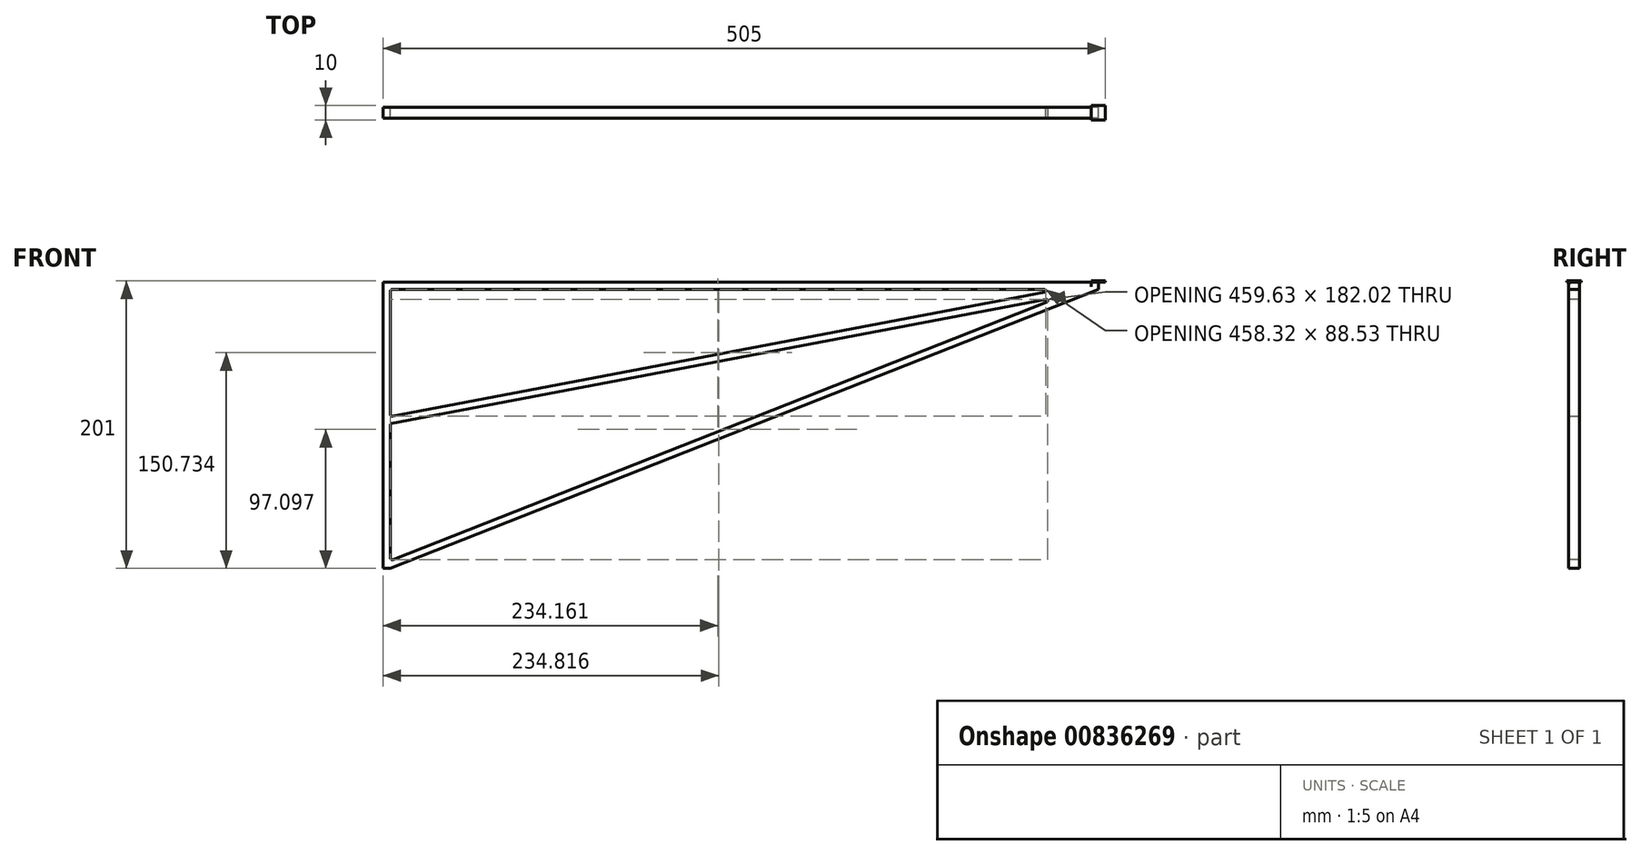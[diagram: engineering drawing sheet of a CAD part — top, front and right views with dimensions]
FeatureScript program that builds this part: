
annotation { "Feature Type Name" : "Feature", "Feature Type Description" : "" }
export const myFeature = defineFeature(function(context is Context, id is Id, definition is map)
    precondition{}
    {
        {
            var Q0;
            Q0=qCreatedBy(makeId("Front.planeOp"),FACE);
            var sketch = newSketch(context, id + "F0", { "sketchPlane" : qUnion([Q0])});
            skLineSegment(sketch, "E0.bottom", {"start": v(-27.04, 0) * mm, "end": v(-495, 0) * mm});
            skLineSegment(sketch, "E0.top", {"start": v(0, 5) * mm, "end": v(-500, 5) * mm});
            skLineSegment(sketch, "E0.left", {"start": v(0, 0) * mm, "end": v(0, 5) * mm});
            skLineSegment(sketch, "E0.right", {"start": v(-500, 0) * mm, "end": v(-500, 5) * mm});
            skLineSegment(sketch, "E1.bottom", {"start": v(-500, 5) * mm, "end": v(-495, 5) * mm});
            skLineSegment(sketch, "E1.top", {"start": v(-500, -195) * mm, "end": v(-495, -195) * mm});
            skLineSegment(sketch, "E1.left", {"start": v(-500, 5) * mm, "end": v(-500, -195) * mm});
            skLineSegment(sketch, "E1.right", {"start": v(-495, 0) * mm, "end": v(-495, -88.84) * mm});
            skLineSegment(sketch, "E2", {"start": v(-495, -195) * mm, "end": v(0, 0) * mm});
            skPoint(sketch, "E3", {"position": v(-495, -189.63) * mm});
            skLineSegment(sketch, "E4", {"start": v(-495, -189.63) * mm, "end": v(-26.11, -4.91) * mm});
            skPoint(sketch, "E5", {"position": v(-147.96, -25.5) * mm});
            skLineSegment(sketch, "E6", {"start": v(-13.64, 0) * mm, "end": v(-14.6, 5) * mm});
            skPoint(sketch, "E7", {"position": v(-14.1, 2.46) * mm});
            skLineSegment(sketch, "E8", {"start": v(-27.04, 0) * mm, "end": v(-495, -88.84) * mm});
            skLineSegment(sketch, "E9", {"start": v(-494.07, -93.76) * mm, "end": v(-26.11, -4.91) * mm});
            skLineSegment(sketch, "E10.trimOffspring", {"start": v(-495, -95.28) * mm, "end": v(-495, -189.63) * mm});
            skLineSegment(sketch, "E11", {"start": v(-408.19, -160.8) * mm, "end": v(-410.02, -156.15) * mm});
            skLineSegment(sketch, "E12", {"start": v(-495, -142.45) * mm, "end": v(-26.11, -4.91) * mm});
            skLineSegment(sketch, "E13", {"start": v(-495, -44.42) * mm, "end": v(-27.04, 0) * mm});
            skLineSegment(sketch, "E14", {"start": v(-495, -95.28) * mm, "end": v(-495, -93.93) * mm});
            skLineSegment(sketch, "E15", {"start": v(-494.07, -93.76) * mm, "end": v(-495, -93.93) * mm});
            skPoint(sketch, "E16.orphan", {"position": v(-495, -93.76) * mm});
            skSolve(sketch);
        }
        {
            var Q0;
            {var subQ6=sQuery(id+"F0.wireOp",EDGE,"E0.bottom");Q0=makeQuery(id+"F0.imprint","IMPRINT",FACE,{"disambiguationData":[TD([[makeQuery(id+"F0.imprint","IMPRINT",EDGE,{"derivedFrom":subQ6}),-1.0]])]});}
            extrude(context, id + "F1", {"entities" : qUnion([Q0]), "depth" : 7.5 * mm, "offsetDistance" : 25 * mm});
        }
        {
            var Q0;
            Q0=makeQuery(id+"F1.opExtrude","SWEPT_EDGE",EDGE,{"disambiguationData":[OSD([sQuery(id+"F0.wireOp",EDGE,"E1.right"),sQuery(id+"F0.wireOp",EDGE,"E8")])]});
            fillet(context, id + "F2", {"entities" : qUnion([Q0]), "radius" : 1.5 * mm, "tangentPropagation" : true, "allowEdgeOverflow" : false});
        }
        {
            var Q0;
            Q0=makeQuery(id+"F1.opExtrude","SWEPT_EDGE",EDGE,{"disambiguationData":[OSD([sQuery(id+"F0.wireOp",EDGE,"E14"),sQuery(id+"F0.wireOp",EDGE,"E15")])]});
            var Q1;
            Q1=makeQuery(id+"F1.opExtrude","SWEPT_EDGE",EDGE,{"disambiguationData":[OSD([sQuery(id+"F0.wireOp",EDGE,"E0.bottom"),sQuery(id+"F0.wireOp",EDGE,"E1.right")])]});
            var Q2;
            Q2=makeQuery(id+"F1.opExtrude","SWEPT_EDGE",EDGE,{"disambiguationData":[OSD([sQuery(id+"F0.wireOp",EDGE,"E4"),sQuery(id+"F0.wireOp",EDGE,"E10.trimOffspring")])]});
            fillet(context, id + "F3", {"entities" : qUnion([Q0, Q1, Q2]), "radius" : 1.5 * mm, "tangentPropagation" : true, "allowEdgeOverflow" : false});
        }
        {
            var Q0;
            Q0=makeQuery(id+"F1.opExtrude","SWEPT_EDGE",EDGE,{"disambiguationData":[OSD([sQuery(id+"F0.wireOp",EDGE,"E4"),sQuery(id+"F0.wireOp",EDGE,"E9"),sQuery(id+"F0.wireOp",EDGE,"E12")])]});
            var Q1;
            Q1=makeQuery(id+"F1.opExtrude","SWEPT_EDGE",EDGE,{"disambiguationData":[OSD([sQuery(id+"F0.wireOp",EDGE,"E0.bottom"),sQuery(id+"F0.wireOp",EDGE,"E8"),sQuery(id+"F0.wireOp",EDGE,"E13")])]});
            fillet(context, id + "F4", {"entities" : qUnion([Q0, Q1]), "radius" : 1 * mm, "tangentPropagation" : true, "allowEdgeOverflow" : false});
        }
        {
            var Q0;
            Q0=makeQuery(id+"F1.opExtrude","SWEPT_FACE",FACE,{"disambiguationData":[OSD([sQuery(id+"F0.wireOp",EDGE,"E0.top"),sQuery(id+"F0.wireOp",EDGE,"E1.bottom")])]});
            var sketch = newSketch(context, id + "F5", { "sketchPlane" : qUnion([Q0])});
            skPoint(sketch, "E17", {"position": v(-5, -8.75) * mm});
            skLineSegment(sketch, "E18.bottom", {"start": v(-5, -8.75) * mm, "end": v(5, -8.75) * mm});
            skLineSegment(sketch, "E18.top", {"start": v(-5, 1.25) * mm, "end": v(5, 1.25) * mm});
            skLineSegment(sketch, "E18.left", {"start": v(-5, -8.75) * mm, "end": v(-5, 1.25) * mm});
            skLineSegment(sketch, "E18.right", {"start": v(5, -8.75) * mm, "end": v(5, 1.25) * mm});
            skSolve(sketch);
        }
        {
            var Q0;
            Q0 = qSketchRegion(id + "F5", true);
            extrude(context, id + "F6", {"entities" : qUnion([Q0]), "operationType" : NewBodyOperationType.ADD, "depth" : 1 * mm, "offsetDistance" : 25 * mm});
        }
        {
            var Q0;
            {var subQ0=sQuery(id+"F0.wireOp",EDGE,"E1.bottom");var subQ1=sQuery(id+"F0.wireOp",EDGE,"E0.top");Q0=makeQuery(id+"F6.boolean.opBoolean","SPLIT",EDGE,{"disambiguationData":[topologyDisambiguationEdgeConnected([makeQuery(id+"F6.opExtrude","CAP_FACE",FACE,{"disambiguationData":[OSD([sQuery(id+"F5.wireOp",EDGE,"E18.bottom"),sQuery(id+"F5.wireOp",EDGE,"E18.top"),sQuery(id+"F5.wireOp",EDGE,"E18.left"),sQuery(id+"F5.wireOp",EDGE,"E18.right")])],"isStart":true})])],"derivedFrom":makeQuery(id+"F1.opExtrude","CAP_EDGE",EDGE,{"disambiguationData":[OSD([subQ1,subQ0])],"isStart":false})});}
            var Q1;
            Q1=makeQuery(id+"F1.opExtrude","SWEPT_EDGE",EDGE,{"disambiguationData":[OSD([sQuery(id+"F0.wireOp",EDGE,"E0.top"),sQuery(id+"F0.wireOp",EDGE,"E0.left")])]});
            var Q2;
            {var subQ0=sQuery(id+"F0.wireOp",EDGE,"E1.bottom");var subQ1=sQuery(id+"F0.wireOp",EDGE,"E0.top");Q2=makeQuery(id+"F6.boolean.opBoolean","SPLIT",EDGE,{"disambiguationData":[topologyDisambiguationEdgeConnected([makeQuery(id+"F6.opExtrude","CAP_FACE",FACE,{"disambiguationData":[OSD([sQuery(id+"F5.wireOp",EDGE,"E18.bottom"),sQuery(id+"F5.wireOp",EDGE,"E18.top"),sQuery(id+"F5.wireOp",EDGE,"E18.left"),sQuery(id+"F5.wireOp",EDGE,"E18.right")])],"isStart":true})])],"derivedFrom":makeQuery(id+"F1.opExtrude","CAP_EDGE",EDGE,{"disambiguationData":[OSD([subQ1,subQ0])],"isStart":true})});}
            fillet(context, id + "F7", {"entities" : qUnion([Q0, Q1, Q2]), "radius" : 3 * mm, "tangentPropagation" : true, "allowEdgeOverflow" : false});
        }
    });
